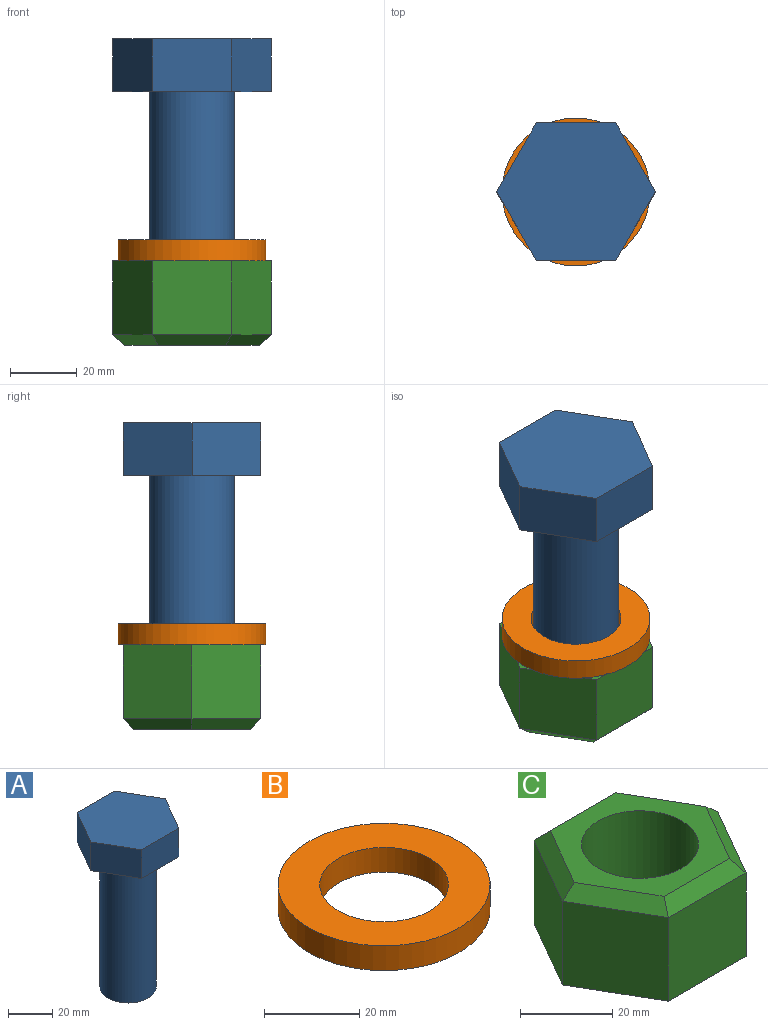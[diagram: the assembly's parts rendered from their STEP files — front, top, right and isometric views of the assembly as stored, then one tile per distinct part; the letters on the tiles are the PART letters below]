
ASSEMBLY  parts=3 mates=2
PART A: 10 faces, bbox 47.7x41.3x92.1 mm
  f0: cylinder r=12.7mm len=76.2mm, axis (0,0,1), area 6080.5mm2, adj f1,f9
  f1: plane 25.4x25.4mm, normal (0,0,-1), area 506.7mm2, adj f0
  f2: plane 20.64x15.88mm, normal (-0.87,0.5,0), area 378.3mm2, adj f3,f7,f8,f9
  f3: plane 20.64x15.88mm, normal (-0.87,-0.5,0), area 378.3mm2, adj f2,f4,f8,f9
  f4: plane 23.83x15.88mm, normal (0,-1,0), area 378.3mm2, adj f3,f5,f8,f9
  f5: plane 20.64x15.88mm, normal (0.87,-0.5,0), area 378.3mm2, adj f4,f6,f8,f9
  f6: plane 20.64x15.88mm, normal (0.87,0.5,0), area 378.3mm2, adj f5,f7,f8,f9
  f7: plane 23.83x15.88mm, normal (0,1,0), area 378.3mm2, adj f2,f6,f8,f9
  f8: plane 47.66x41.28mm, normal (0,0,1), area 1475.4mm2, adj f2,f3,f4,f5,f6,f7
  f9: plane 47.66x41.28mm, normal (0,0,-1), area 968.7mm2, adj f0,f2,f3,f4,f5,f6,f7
PART B: 4 faces, bbox 44.5x44.5x6.4 mm
  f0: cylinder r=13.49mm len=26.99mm, axis (0,0,-1), area 538.4mm2, adj f2,f3
  f1: cylinder r=22.23mm len=44.45mm, axis (0,0,-1), area 886.7mm2, adj f2,f3
  f2: plane 44.45x44.45mm, normal (0,0,1), area 979.8mm2, adj f0,f1
  f3: plane 44.45x44.45mm, normal (0,0,-1), area 979.8mm2, adj f0,f1
PART C: 15 faces, bbox 47.7x41.3x25.4 mm
  f0: plane 22.23x20.64mm, normal (-0.87,0.5,0), area 529.6mm2, adj f1,f6,f8,f9
  f1: plane 22.23x20.64mm, normal (-0.87,-0.5,0), area 529.6mm2, adj f0,f2,f8,f11
  f2: plane 23.83x22.23mm, normal (0,-1,0), area 529.6mm2, adj f1,f3,f8,f13
  f3: plane 22.23x20.64mm, normal (0.87,-0.5,0), area 529.6mm2, adj f2,f4,f8,f14
  f4: plane 22.23x20.64mm, normal (0.87,0.5,0), area 529.6mm2, adj f3,f6,f8,f12
  f5: cylinder r=12.7mm len=25.4mm, axis (0,0,-1), area 2026.8mm2, adj f7,f8
  f6: plane 23.83x22.23mm, normal (0,1,0), area 529.6mm2, adj f0,f4,f8,f10
  f7: plane 40.33x34.93mm, normal (0,0,1), area 549.6mm2, adj f5,f9,f10,f11,f12,f13,f14
  f8: plane 47.66x41.28mm, normal (0,0,-1), area 968.7mm2, adj f0,f1,f2,f3,f4,f5,f6
  f9: plane 20.64x13.75mm, normal (-0.61,0.35,0.71), area 98.8mm2, adj f0,f7,f10,f11
  f10: plane 23.83x3.18mm, normal (0,0.71,0.71), area 98.8mm2, adj f6,f7,f9,f12
  f11: plane 20.64x13.75mm, normal (-0.61,-0.35,0.71), area 98.8mm2, adj f1,f7,f9,f13
  f12: plane 20.64x13.75mm, normal (0.61,0.35,0.71), area 98.8mm2, adj f4,f7,f10,f14
  f13: plane 23.83x3.18mm, normal (0,-0.71,0.71), area 98.8mm2, adj f2,f7,f11,f14
  f14: plane 20.64x13.75mm, normal (0.61,-0.35,0.71), area 98.8mm2, adj f3,f7,f12,f13
PLACE A t=(0,0,1.59)mm
PLACE B t=(0,0,1.59)mm
PLACE C rot(axis=(0,1,0),180deg) t=(0,0,1.59)mm
MATE fastened C.f5 <-> B.f0  axis (0,0,1) through (0,0,1.59)mm
MATE fastened B.f0 <-> A.f0  axis (0,0,1) through (0,0,7.94)mm
